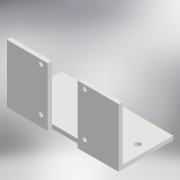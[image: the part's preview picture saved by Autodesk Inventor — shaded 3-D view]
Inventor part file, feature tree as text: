
AUTODESK INVENTOR PART (.ipt)
format: ipt  version: 2021 (Build 250183000, 183)  size: 152,064 bytes
history: native  units: mm
features: extrude x4, thicken_offset x4, sketch x4, mirror x1
ambient origin geometry x8: Origin, YZ Plane, XZ Plane, XY Plane, X Axis, Y Axis, Z Axis, Center Point
bodies: Solid1 (feature_tree)
feature tree (13):
  extrude  "Extrusion1"  Depth=37.0mm
  extrude  "Extrusion2"  Depth=10.0mm
  extrude  "Extrusion3"  Depth=3.0mm TaperAngle=0.0deg
  thicken_offset  "Thicken2"
  mirror  "Mirror3"
  thicken_offset  "Thicken3"
  extrude  "Extrusion6"  Depth=3.0mm
  thicken_offset  "Thicken4"
  thicken_offset  "Thicken5"
  sketch  "Sketch1"  dims[d0=42.0mm d1=37.0mm]
  sketch  "Sketch2"  dims[d2=3.0mm d3=0.0mm d4=10.0mm]
  sketch  "Sketch3"  dims[d5=45.0mm d6=3.0mm d7=0.0mm]
  sketch  "Sketch8"  dims[d8=3.0mm d9=3.0mm d10=3.0mm d11=0.0mm d17=20.0mm d18=10.0mm d22=20.0mm d23=10.0mm d26=10.0mm d27=0.0mm d28=4.0mm d29=4.0mm d30=2.0mm d31=2.0mm d32=2.0mm d33=2.0mm]
